FCSTD DOCUMENT  (FreeCAD 0.19R24291 (Git))
Label: P11 orthographic
License: All rights reserved
LicenseURL: http://en.wikipedia.org/wiki/All_rights_reserved
objects: Part::Part2DObjectPython×25, App::FeaturePython×17
note: 25 computed .brp shape members not serialized (recipe doc carries the construction recipe); baked Part::Feature solids carry a one-line shape summary decoded from their .brp

FEATURE [App::FeaturePython] Text  # WARN: FeaturePython — macro-defined, semantics opaque (R4)
  Placement = pos=(-24.6768,-10.844,0) rot=(0,0,1;0rad)
  Text = Right Side View
FEATURE [Part::Part2DObjectPython] Line001  # Draft 2D object (typed FeaturePython)
  Area = 0
  ChamferSize = 0
  Closed = false
  End = (-30,20,0)
  FilletRadius = 0
  Length = 20
  MakeFace = false
  Placement = pos=(-30,-2.8e-15,0) rot=(0,0,1;0rad)
  Points = (2) [(0,0,0),(0,20,0)]
  Start = (-30,-2.8e-15,0)
  Subdivisions = 0
FEATURE [Part::Part2DObjectPython] Line002  # Draft 2D object (typed FeaturePython)
  Area = 0
  ChamferSize = 0
  Closed = false
  End = (0,20,0)
  FilletRadius = 0
  Length = 20
  MakeFace = false
  Points = (2) [(0,-2.75546e-15,0),(0,20,0)]
  Start = (0,-2.8e-15,0)
  Subdivisions = 0
FEATURE [Part::Part2DObjectPython] Line004  # Draft 2D object (typed FeaturePython)
  Area = 0
  ChamferSize = 0
  Closed = false
  End = (-30,10,0)
  FilletRadius = 0
  Length = 30
  MakeFace = false
  Points = (2) [(-6.12323e-16,10,0),(-30,10,0)]
  Start = (-6e-16,10,0)
  Subdivisions = 0
FEATURE [Part::Part2DObjectPython] Line005  # Draft 2D object (typed FeaturePython)
  Area = 0
  ChamferSize = 0
  Closed = false
  End = (-15,-1.8e-15,0)
  FilletRadius = 0
  Length = 10
  MakeFace = false
  Placement = pos=(-15,10,0) rot=(0,0,1;0rad)
  Points = (2) [(0,0,0),(0,-10,0)]
  Start = (-15,10,0)
  Subdivisions = 0
FEATURE [Part::Part2DObjectPython] Line006  # Draft 2D object (typed FeaturePython)
  Area = 0
  ChamferSize = 0
  Closed = false
  End = (17.6028,-44.3212,0)
  FilletRadius = 0
  Length = 30
  MakeFace = false
  Placement = pos=(17.6028,20,0) rot=(0,0,1;0rad)
  Points = (2) [(1.42109e-14,-34.3212,0),(3.55271e-14,-64.3212,0)]
  Start = (17.6028,-14.3212,0)
  Subdivisions = 0
FEATURE [Part::Part2DObjectPython] Line009  # Draft 2D object (typed FeaturePython)
  Area = 0
  ChamferSize = 0
  Closed = false
  End = (42.6028,10,0)
  FilletRadius = 0
  Length = 15
  MakeFace = false
  Placement = pos=(32.6028,10,0) rot=(0,0,1;0rad)
  Points = (2) [(-5,3.55271e-15,0),(10,3.55271e-15,0)]
  Start = (27.6028,10,0)
  Subdivisions = 0
FEATURE [Part::Part2DObjectPython] Line010  # Draft 2D object (typed FeaturePython)
  Area = 0
  ChamferSize = 0
  Closed = false
  End = (27.6028,-44.3212,0)
  FilletRadius = 0
  Length = 30
  MakeFace = false
  Placement = pos=(27.6028,10,0) rot=(0,0,1;0rad)
  Points = (2) [(1.06581e-14,-24.3212,0),(2.13163e-14,-54.3212,0)]
  Start = (27.6028,-14.3212,0)
  Subdivisions = 0
FEATURE [Part::Part2DObjectPython] Line011  # Draft 2D object (typed FeaturePython)
  Area = 0
  ChamferSize = 0
  Closed = false
  End = (42.6028,3.6e-15,0)
  FilletRadius = 0
  Length = 10
  MakeFace = false
  Placement = pos=(42.6028,10,0) rot=(0,0,1;0rad)
  Points = (2) [(0,0,0),(0,-10,0)]
  Start = (42.6028,10,0)
  Subdivisions = 0
FEATURE [Part::Part2DObjectPython] Line  # Draft 2D object (typed FeaturePython)
  Area = 0
  ChamferSize = 0
  Closed = false
  End = (0,20,0)
  FilletRadius = 0
  Length = 30
  MakeFace = false
  Placement = pos=(-30,20,0) rot=(0,0,1;0rad)
  Points = (2) [(0,0,0),(30,0,0)]
  Start = (-30,20,0)
  Subdivisions = 0
FEATURE [Part::Part2DObjectPython] Line012  # Draft 2D object (typed FeaturePython)
  Area = 0
  ChamferSize = 0
  Closed = false
  End = (0,-2.8e-15,0)
  FilletRadius = 0
  Length = 30
  MakeFace = false
  Placement = pos=(-30,-2.8e-15,0) rot=(0,0,1;0rad)
  Points = (2) [(0,0,0),(30,-9.18485e-16,0)]
  Start = (-30,-2.8e-15,0)
  Subdivisions = 0
FEATURE [Part::Part2DObjectPython] Line013  # Draft 2D object (typed FeaturePython)
  Area = 0
  ChamferSize = 0
  Closed = false
  End = (27.6028,20,0)
  FilletRadius = 0
  Length = 10
  MakeFace = false
  Placement = pos=(17.6028,20,0) rot=(0,0,1;0rad)
  Points = (2) [(0,0,0),(10,0,0)]
  Start = (17.6028,20,0)
  Subdivisions = 0
FEATURE [Part::Part2DObjectPython] Line014  # Draft 2D object (typed FeaturePython)
  Area = 0
  ChamferSize = 0
  Closed = false
  End = (42.6028,3.6e-15,0)
  FilletRadius = 0
  Length = 25
  MakeFace = false
  Placement = pos=(17.6028,0,0) rot=(0,0,1;0rad)
  Points = (2) [(0,0,0),(25,2.78731e-15,0)]
  Start = (17.6028,0,0)
  Subdivisions = 0
FEATURE [Part::Part2DObjectPython] Line015  # Draft 2D object (typed FeaturePython)
  Area = 0
  ChamferSize = 0
  Closed = false
  End = (17.6028,-14.3212,0)
  FilletRadius = 0
  Length = 25
  MakeFace = false
  Placement = pos=(17.6028,-14.3212,0) rot=(0,0,1;0rad)
  Points = (2) [(25,5.32907e-15,0),(0,0,0)]
  Start = (42.6028,-14.3212,0)
  Subdivisions = 0
FEATURE [Part::Part2DObjectPython] Line016  # Draft 2D object (typed FeaturePython)
  Area = 0
  ChamferSize = 0
  Closed = false
  End = (17.6028,-44.3212,0)
  FilletRadius = 0
  Length = 15
  MakeFace = false
  Points = (2) [(32.6028,-44.3212,0),(17.6028,-44.3212,0)]
  Start = (32.6028,-44.3212,0)
  Subdivisions = 0
FEATURE [Part::Part2DObjectPython] Line017  # Draft 2D object (typed FeaturePython)
  Area = 0
  ChamferSize = 0
  Closed = false
  End = (42.6028,-29.3212,0)
  FilletRadius = 0
  Length = 15
  MakeFace = false
  Placement = pos=(42.6028,-14.3212,0) rot=(0,0,1;0rad)
  Points = (2) [(0,0,0),(0,-15,0)]
  Start = (42.6028,-14.3212,0)
  Subdivisions = 0
FEATURE [Part::Part2DObjectPython] Line018  # Draft 2D object (typed FeaturePython)
  Area = 0
  ChamferSize = 0
  Closed = false
  End = (32.6028,-29.3212,0)
  FilletRadius = 0
  Length = 10
  MakeFace = false
  Placement = pos=(42.6028,-29.3212,0) rot=(0,0,1;0rad)
  Points = (2) [(0,0,0),(-10,-7.10543e-15,0)]
  Start = (42.6028,-29.3212,0)
  Subdivisions = 0
FEATURE [Part::Part2DObjectPython] Line019  # Draft 2D object (typed FeaturePython)
  Area = 0
  ChamferSize = 0
  Closed = false
  End = (32.6028,10,0)
  FilletRadius = 0
  Length = 10
  MakeFace = false
  Placement = pos=(32.6028,2.1e-15,0) rot=(0,0,1;0rad)
  Points = (2) [(0,0,0),(-7.10543e-15,10,0)]
  Start = (32.6028,2.1e-15,0)
  Subdivisions = 0
FEATURE [Part::Part2DObjectPython] Line020  # Draft 2D object (typed FeaturePython)
  Area = 0
  ChamferSize = 0
  Closed = false
  End = (32.6028,-44.3212,0)
  FilletRadius = 0
  Length = 15
  MakeFace = false
  Placement = pos=(32.6028,-29.3212,0) rot=(0,0,1;0rad)
  Points = (2) [(0,0,0),(0,-15,0)]
  Start = (32.6028,-29.3212,0)
  Subdivisions = 0
FEATURE [Part::Part2DObjectPython] Line021  # Draft 2D object (typed FeaturePython)
  Area = 0
  ChamferSize = 0
  Closed = false
  End = (17.6028,20,0)
  FilletRadius = 0
  Length = 20
  MakeFace = false
  Placement = pos=(17.6028,0,0) rot=(0,0,1;0rad)
  Points = (2) [(0,0,0),(0,20,0)]
  Start = (17.6028,0,0)
  Subdivisions = 0
FEATURE [Part::Part2DObjectPython] Line022  # Draft 2D object (typed FeaturePython)
  Area = 0
  ChamferSize = 0
  Closed = false
  End = (27.6028,10,0)
  FilletRadius = 0
  Length = 10
  MakeFace = false
  Placement = pos=(27.6028,20,0) rot=(0,0,1;0rad)
  Points = (2) [(0,0,0),(3.55271e-15,-10,0)]
  Start = (27.6028,20,0)
  Subdivisions = 0
FEATURE [App::FeaturePython] Text001  # WARN: FeaturePython — macro-defined, semantics opaque (R4)
  Placement = pos=(21.8917,-7.89583,0) rot=(0,0,1;0rad)
  Text = Front View
FEATURE [App::FeaturePython] Text002  # WARN: FeaturePython — macro-defined, semantics opaque (R4)
  Placement = pos=(24.571,-54.0009,0) rot=(0,0,1;0rad)
  Text = Top View
FEATURE [App::FeaturePython] Dimension  # Draft dimension (typed FeaturePython)
  Diameter = false
  Dimline = (-34.3721,-3e-15,0)
  Direction = (0,0,0)
  Distance = 20
  End = (-30,-2.8e-15,0)
  Normal = (0,0,1)
  Start = (-30,20,0)
FEATURE [App::FeaturePython] Dimension001  # Draft dimension (typed FeaturePython)
  Diameter = false
  Dimline = (-30,-4,0)
  Direction = (0,0,0)
  Distance = 15
  End = (-30,-1.8e-15,0)
  Normal = (0,0,1)
  Start = (-15,-1.8e-15,0)
FEATURE [App::FeaturePython] Dimension002  # Draft dimension (typed FeaturePython)
  Diameter = false
  Dimline = (0,-4,0)
  Direction = (0,0,0)
  Distance = 15
  End = (0,-1.8e-15,0)
  Normal = (0,0,1)
  Start = (-15,-1.8e-15,0)
FEATURE [App::FeaturePython] Dimension003  # Draft dimension (typed FeaturePython)
  Diameter = false
  Dimline = (0,24,0)
  Direction = (0,0,0)
  Distance = 30
  End = (0,20,0)
  Normal = (0,0,1)
  Start = (-30,20,0)
FEATURE [App::FeaturePython] Dimension004  # Draft dimension (typed FeaturePython)
  Diameter = false
  Dimline = (27.6028,24,0)
  Direction = (0,0,0)
  Distance = 10
  End = (27.6028,20,0)
  Normal = (0,0,1)
  Start = (17.6028,20,0)
FEATURE [App::FeaturePython] Dimension006  # Draft dimension (typed FeaturePython)
  Diameter = false
  Dimline = (51.6028,2.1e-15,0)
  Direction = (0,0,0)
  Distance = 20
  End = (17.6028,0,0)
  Normal = (0,0,1)
  Start = (17.6028,20,0)
FEATURE [App::FeaturePython] Dimension007  # Draft dimension (typed FeaturePython)
  Diameter = false
  Dimline = (45.6028,3.7e-15,0)
  Direction = (0,0,0)
  Distance = 10
  End = (42.6028,3.6e-15,0)
  Normal = (0,0,1)
  Start = (42.6028,10,0)
FEATURE [App::FeaturePython] Dimension008  # Draft dimension (typed FeaturePython)
  Diameter = false
  Dimline = (42.6028,-4,0)
  Direction = (0,0,0)
  Distance = 25
  End = (42.6028,3.6e-15,0)
  Normal = (0,0,1)
  Start = (17.6028,0,0)
FEATURE [App::FeaturePython] Dimension011  # Draft dimension (typed FeaturePython)
  Diameter = false
  Dimline = (27.6028,-48.3212,0)
  Direction = (0,0,0)
  Distance = 10
  End = (27.6028,-44.3212,0)
  Normal = (0,0,1)
  Start = (17.6028,-44.3212,0)
FEATURE [App::FeaturePython] Dimension012  # Draft dimension (typed FeaturePython)
  Diameter = false
  Dimline = (32.6028,-48.3212,0)
  Direction = (0,0,0)
  Distance = 5
  End = (32.6028,-44.3212,0)
  Normal = (0,0,1)
  Start = (27.6028,-44.3212,0)
FEATURE [App::FeaturePython] Dimension013  # Draft dimension (typed FeaturePython)
  Diameter = false
  Dimline = (45.6028,-29.3212,0)
  Direction = (0,0,0)
  Distance = 15
  End = (42.6028,-29.3212,0)
  Normal = (0,0,1)
  Start = (42.6028,-14.3212,0)
FEATURE [App::FeaturePython] Dimension014  # Draft dimension (typed FeaturePython)
  Diameter = false
  Dimline = (40.4555,14.2069,0)
  Direction = (0,0,0)
  Distance = 10
  End = (42.6028,10,0)
  Normal = (0,0,1)
  Start = (32.6028,10,0)
FEATURE [Part::Part2DObjectPython] Line023  # Draft 2D object (typed FeaturePython)
  Area = 0
  ChamferSize = 0
  Closed = false
  End = (17.6028,20,0)
  FilletRadius = 0
  Length = 17.6028
  MakeFace = false
  Placement = pos=(0,20,0) rot=(0,0,1;0rad)
  Points = (2) [(0,0,0),(17.6028,0,0)]
  Start = (0,20,0)
  Subdivisions = 0
FEATURE [Part::Part2DObjectPython] Line024  # Draft 2D object (typed FeaturePython)
  Area = 0
  ChamferSize = 0
  Closed = false
  End = (17.6028,10,0)
  FilletRadius = 0
  Length = 17.6028
  MakeFace = false
  Placement = pos=(0,10,0) rot=(0,0,1;0rad)
  Points = (2) [(0,0,0),(17.6028,3.55271e-15,0)]
  Start = (0,10,0)
  Subdivisions = 0
FEATURE [Part::Part2DObjectPython] Line025  # Draft 2D object (typed FeaturePython)
  Area = 0
  ChamferSize = 0
  Closed = false
  End = (17.6028,0,0)
  FilletRadius = 0
  Length = 17.6028
  MakeFace = false
  Placement = pos=(0,-2.8e-15,0) rot=(0,0,1;0rad)
  Points = (2) [(0,0,0),(17.6028,2.21652e-15,0)]
  Start = (0,-2.8e-15,0)
  Subdivisions = 0
FEATURE [Part::Part2DObjectPython] Line026  # Draft 2D object (typed FeaturePython)
  Area = 0
  ChamferSize = 0
  Closed = false
  End = (17.6028,-14.3212,0)
  FilletRadius = 0
  Length = 14.3212
  MakeFace = false
  Placement = pos=(17.6028,0,0) rot=(0,0,1;0rad)
  Points = (2) [(0,0,0),(7.10543e-15,-14.3212,0)]
  Start = (17.6028,0,0)
  Subdivisions = 0
FEATURE [Part::Part2DObjectPython] Line027  # Draft 2D object (typed FeaturePython)
  Area = 0
  ChamferSize = 0
  Closed = false
  End = (42.6028,-14.3212,0)
  FilletRadius = 0
  Length = 14.3212
  MakeFace = false
  Placement = pos=(42.6028,4e-15,0) rot=(0,0,1;0rad)
  Points = (2) [(0,0,0),(7.10543e-15,-14.3212,0)]
  Start = (42.6028,4e-15,0)
  Subdivisions = 0
FEATURE [App::FeaturePython] Dimension015  # Draft dimension (typed FeaturePython)
  Diameter = false
  Dimline = (51.4999,0.571838,0)
  Direction = (0,0,0)
  Distance = 30
  End = (17.6028,-44.3212,0)
  Normal = (0,0,1)
  Start = (17.6028,-14.3212,0)
FEATURE [App::FeaturePython] Text003  # WARN: FeaturePython — macro-defined, semantics opaque (R4)
  Placement = pos=(-13.2662,-59.8353,0) rot=(0,0,1;0rad)
  Text = All Dimensions are in mm
